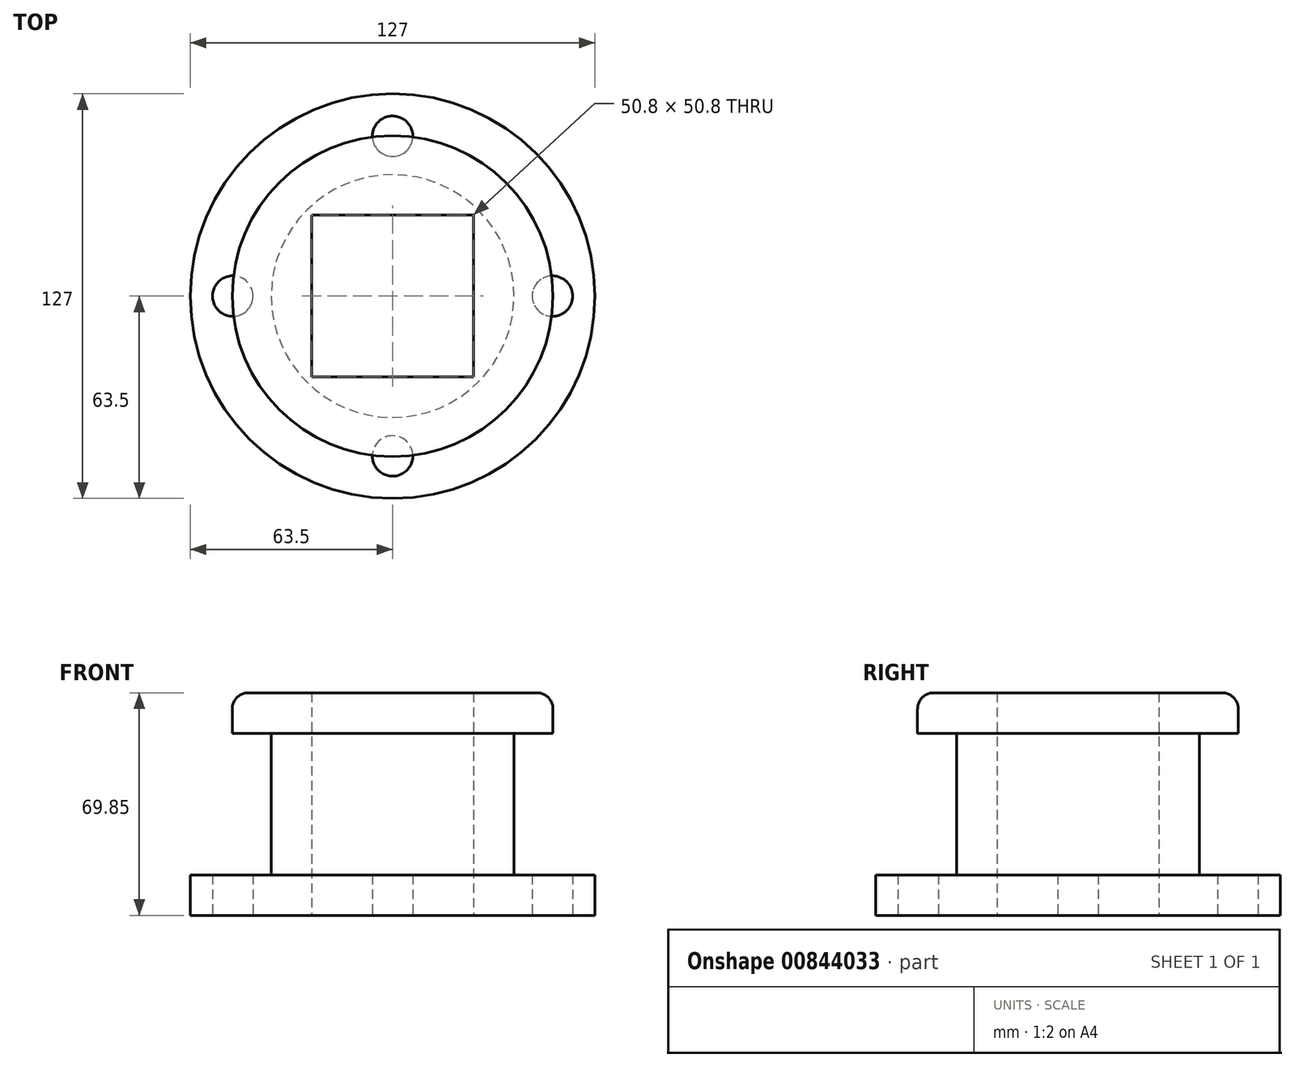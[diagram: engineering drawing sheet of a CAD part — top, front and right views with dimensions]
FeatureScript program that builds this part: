
annotation { "Feature Type Name" : "Feature", "Feature Type Description" : "" }
export const myFeature = defineFeature(function(context is Context, id is Id, definition is map)
    precondition{}
    {
        {
            var Q0;
            Q0=qCreatedBy(makeId("Top.planeOp"),FACE);
            var sketch = newSketch(context, id + "F0", { "sketchPlane" : qUnion([Q0])});
            skCircle(sketch, "E0", {"center": v(0, 0) * mm, "radius": 63.5 * mm});
            skSolve(sketch);
        }
        {
            var Q0;
            Q0=makeQuery(id+"F0.imprint","IMPRINT",FACE,{"disambiguationData":[TD([[makeQuery(id+"F0.imprint","IMPRINT",EDGE,{"derivedFrom":sQuery(id+"F0.wireOp",EDGE,"E0")}),1.0]])]});
            extrude(context, id + "F1", {"entities" : qUnion([Q0]), "depth" : 12.7 * mm, "offsetDistance" : 25.4 * mm});
        }
        {
            var Q0;
            Q0=qCreatedBy(makeId("Top.planeOp"),FACE);
            var sketch = newSketch(context, id + "F2", { "sketchPlane" : qUnion([Q0])});
            skCircle(sketch, "E1", {"center": v(0, 0) * mm, "radius": 38.1 * mm});
            skSolve(sketch);
        }
        {
            var Q0;
            Q0 = qSketchRegion(id + "F2", true);
            extrude(context, id + "F3", {"entities" : qUnion([Q0]), "operationType" : NewBodyOperationType.ADD, "depth" : 57.15 * mm, "offsetDistance" : 25.4 * mm});
        }
        {
            var Q0;
            Q0=makeQuery(id+"F3.opExtrude","CAP_FACE",FACE,{"disambiguationData":[OSD([sQuery(id+"F2.wireOp",EDGE,"E1")])],"isStart":false});
            var sketch = newSketch(context, id + "F4", { "sketchPlane" : qUnion([Q0])});
            skCircle(sketch, "E2", {"center": v(0, 0) * mm, "radius": 50.34 * mm});
            skSolve(sketch);
        }
        {
            var Q0;
            Q0 = qSketchRegion(id + "F4", true);
            extrude(context, id + "F5", {"entities" : qUnion([Q0]), "operationType" : NewBodyOperationType.ADD, "depth" : 12.7 * mm, "offsetDistance" : 25.4 * mm});
        }
        {
            var Q0;
            Q0=makeQuery(id+"F5.opExtrude","CAP_FACE",FACE,{"disambiguationData":[OSD([sQuery(id+"F4.wireOp",EDGE,"E2")])],"isStart":false});
            fillet(context, id + "F6", {"entities" : qUnion([Q0]), "radius" : 5.08 * mm, "tangentPropagation" : true, "allowEdgeOverflow" : false});
        }
        {
            var Q0;
            Q0=qCreatedBy(makeId("Top.planeOp"),FACE);
            var sketch = newSketch(context, id + "F7", { "sketchPlane" : qUnion([Q0])});
            skCircle(sketch, "E3", {"center": v(0, 50.17) * mm, "radius": 6.35 * mm});
            skCircle(sketch, "E4.1.0", {"center": v(-50.17, 0) * mm, "radius": 6.35 * mm});
            skCircle(sketch, "E4.2.0", {"center": v(0, -50.17) * mm, "radius": 6.35 * mm});
            skCircle(sketch, "E4.3.0", {"center": v(50.17, 0) * mm, "radius": 6.35 * mm});
            skPoint(sketch, "E4.center", {"position": v(0, 0) * mm});
            skSolve(sketch);
        }
        {
            var Q0;
            Q0 = qSketchRegion(id + "F7", true);
            extrude(context, id + "F8", {"entities" : qUnion([Q0]), "operationType" : NewBodyOperationType.REMOVE, "depth" : 12.7 * mm, "offsetDistance" : 25.4 * mm});
        }
        {
            var Q0;
            Q0=qCreatedBy(makeId("Top.planeOp"),FACE);
            var sketch = newSketch(context, id + "F9", { "sketchPlane" : qUnion([Q0])});
            skLineSegment(sketch, "E5.bottom", {"start": v(25.4, 25.4) * mm, "end": v(-25.4, 25.4) * mm});
            skLineSegment(sketch, "E5.top", {"start": v(25.4, -25.4) * mm, "end": v(-25.4, -25.4) * mm});
            skLineSegment(sketch, "E5.left", {"start": v(25.4, 25.4) * mm, "end": v(25.4, -25.4) * mm});
            skLineSegment(sketch, "E5.right", {"start": v(-25.4, 25.4) * mm, "end": v(-25.4, -25.4) * mm});
            skPoint(sketch, "E5.middle", {"position": v(0, 0) * mm});
            skSolve(sketch);
        }
        {
            var Q0;
            Q0=makeQuery(id+"F9.imprint","IMPRINT",FACE,{"disambiguationData":[TD([[makeQuery(id+"F9.imprint","IMPRINT",EDGE,{"derivedFrom":sQuery(id+"F9.wireOp",EDGE,"E5.bottom")}),1.0]])]});
            extrude(context, id + "F10", {"entities" : qUnion([Q0]), "operationType" : NewBodyOperationType.REMOVE, "depth" : 127 * mm, "offsetDistance" : 25.4 * mm});
        }
    });
